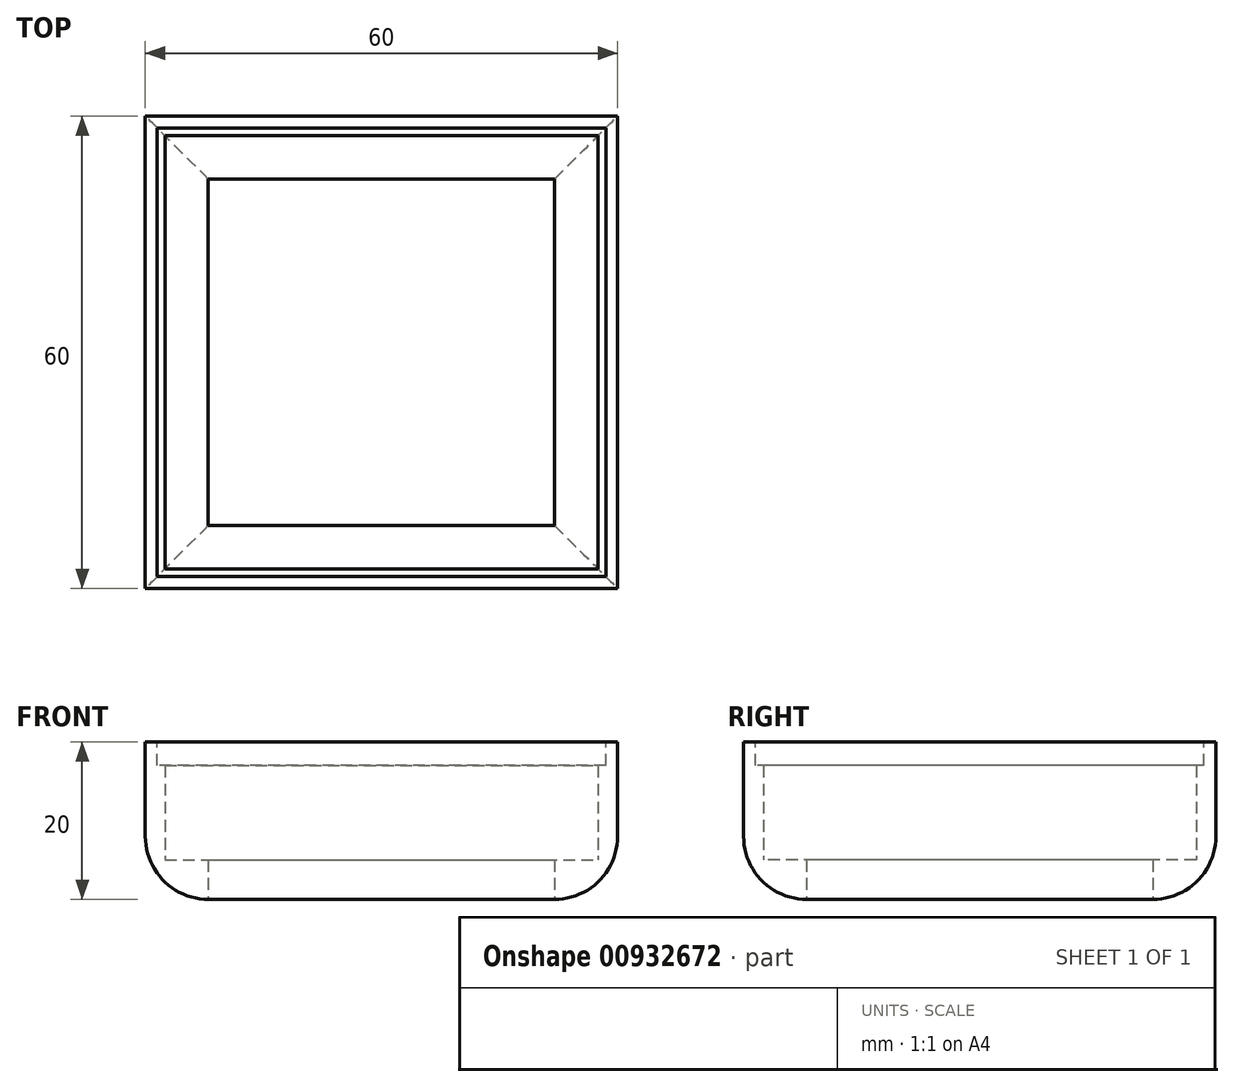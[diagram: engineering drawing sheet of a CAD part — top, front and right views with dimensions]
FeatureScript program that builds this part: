
annotation { "Feature Type Name" : "Feature", "Feature Type Description" : "" }
export const myFeature = defineFeature(function(context is Context, id is Id, definition is map)
    precondition{}
    {
        {
            var Q0;
            Q0=qCreatedBy(makeId("Top.planeOp"),FACE);
            var sketch = newSketch(context, id + "F0", { "sketchPlane" : qUnion([Q0])});
            skLineSegment(sketch, "E0.bottom", {"start": v(-30, 30) * mm, "end": v(30, 30) * mm});
            skLineSegment(sketch, "E0.top", {"start": v(-30, -30) * mm, "end": v(30, -30) * mm});
            skLineSegment(sketch, "E0.left", {"start": v(-30, 30) * mm, "end": v(-30, -30) * mm});
            skLineSegment(sketch, "E0.right", {"start": v(30, 30) * mm, "end": v(30, -30) * mm});
            skPoint(sketch, "E0.middle", {"position": v(0, 0) * mm});
            skLineSegment(sketch, "E1.bottom", {"start": v(-27.5, 27.5) * mm, "end": v(27.5, 27.5) * mm});
            skLineSegment(sketch, "E1.top", {"start": v(-27.5, -27.5) * mm, "end": v(27.5, -27.5) * mm});
            skLineSegment(sketch, "E1.left", {"start": v(-27.5, 27.5) * mm, "end": v(-27.5, -27.5) * mm});
            skLineSegment(sketch, "E1.right", {"start": v(27.5, 27.5) * mm, "end": v(27.5, -27.5) * mm});
            skSolve(sketch);
        }
        {
            var Q0;
            Q0=makeQuery(id+"F0.imprint","IMPRINT",FACE,{"disambiguationData":[TD([[makeQuery(id+"F0.imprint","IMPRINT",EDGE,{"derivedFrom":sQuery(id+"F0.wireOp",EDGE,"E0.bottom")}),-1.0]])]});
            extrude(context, id + "F1", {"entities" : qUnion([Q0]), "depth" : 15 * mm, "offsetDistance" : 25 * mm});
        }
        {
            var Q0;
            Q0=makeQuery(id+"F1.opExtrude","CAP_FACE",FACE,{"disambiguationData":[OSD([sQuery(id+"F0.wireOp",EDGE,"E0.bottom"),sQuery(id+"F0.wireOp",EDGE,"E0.top"),sQuery(id+"F0.wireOp",EDGE,"E0.left"),sQuery(id+"F0.wireOp",EDGE,"E0.right"),sQuery(id+"F0.wireOp",EDGE,"E1.bottom"),sQuery(id+"F0.wireOp",EDGE,"E1.top"),sQuery(id+"F0.wireOp",EDGE,"E1.left"),sQuery(id+"F0.wireOp",EDGE,"E1.right")])],"isStart":true});
            var sketch = newSketch(context, id + "F2", { "sketchPlane" : qUnion([Q0])});
            skLineSegment(sketch, "E2.bottom", {"start": v(30, -30) * mm, "end": v(-30, -30) * mm});
            skLineSegment(sketch, "E2.top", {"start": v(30, 30) * mm, "end": v(-30, 30) * mm});
            skLineSegment(sketch, "E2.left", {"start": v(30, -30) * mm, "end": v(30, 30) * mm});
            skLineSegment(sketch, "E2.right", {"start": v(-30, -30) * mm, "end": v(-30, 30) * mm});
            skSolve(sketch);
        }
        {
            var Q0;
            Q0=makeQuery(id+"F2.imprint","IMPRINT",FACE,{"disambiguationData":[TD([[makeQuery(id+"F2.imprint","IMPRINT",EDGE,{"derivedFrom":sQuery(id+"F2.wireOp",EDGE,"E2.bottom")}),1.0]])]});
            var Q1;
            Q1=makeQuery(id+"F2.imprint","IMPRINT",FACE,{"disambiguationData":[TD([[makeQuery(id+"F2.imprint","IMPRINT",EDGE,{"derivedFrom":makeQuery(id+"F1.opExtrude","CAP_EDGE",EDGE,{"disambiguationData":[OSD([sQuery(id+"F0.wireOp",EDGE,"E1.bottom")])],"isStart":true})}),1.0]])]});
            extrude(context, id + "F3", {"entities" : qUnion([Q0, Q1]), "operationType" : NewBodyOperationType.ADD, "depth" : 5 * mm, "offsetDistance" : 25 * mm});
        }
        {
            var Q0;
            Q0=makeQuery(id+"F1.opExtrude","CAP_FACE",FACE,{"disambiguationData":[OSD([sQuery(id+"F0.wireOp",EDGE,"E0.bottom"),sQuery(id+"F0.wireOp",EDGE,"E0.top"),sQuery(id+"F0.wireOp",EDGE,"E0.left"),sQuery(id+"F0.wireOp",EDGE,"E0.right"),sQuery(id+"F0.wireOp",EDGE,"E1.bottom"),sQuery(id+"F0.wireOp",EDGE,"E1.top"),sQuery(id+"F0.wireOp",EDGE,"E1.left"),sQuery(id+"F0.wireOp",EDGE,"E1.right")])],"isStart":false});
            var sketch = newSketch(context, id + "F4", { "sketchPlane" : qUnion([Q0])});
            skLineSegment(sketch, "E3.bottom", {"start": v(28.5, 28.5) * mm, "end": v(-28.5, 28.5) * mm});
            skLineSegment(sketch, "E3.top", {"start": v(28.5, -28.5) * mm, "end": v(-28.5, -28.5) * mm});
            skLineSegment(sketch, "E3.left", {"start": v(28.5, 28.5) * mm, "end": v(28.5, -28.5) * mm});
            skLineSegment(sketch, "E3.right", {"start": v(-28.5, 28.5) * mm, "end": v(-28.5, -28.5) * mm});
            skPoint(sketch, "E3.middle", {"position": v(0, 0) * mm});
            skSolve(sketch);
        }
        {
            var Q0;
            Q0=makeQuery(id+"F4.imprint","IMPRINT",FACE,{"disambiguationData":[TD([[makeQuery(id+"F4.imprint","IMPRINT",EDGE,{"derivedFrom":sQuery(id+"F4.wireOp",EDGE,"E3.bottom")}),1.0]])]});
            extrude(context, id + "F5", {"entities" : qUnion([Q0]), "operationType" : NewBodyOperationType.REMOVE, "oppositeDirection" : true, "depth" : 3 * mm, "offsetDistance" : 25 * mm});
        }
        {
            var Q0;
            Q0=makeQuery(id+"F3.opExtrude","CAP_EDGE",EDGE,{"disambiguationData":[OSD([sQuery(id+"F2.wireOp",EDGE,"E2.right")])],"isStart":false});
            var Q1;
            Q1=makeQuery(id+"F3.opExtrude","CAP_EDGE",EDGE,{"disambiguationData":[OSD([sQuery(id+"F2.wireOp",EDGE,"E2.left")])],"isStart":false});
            var Q2;
            Q2=makeQuery(id+"F3.opExtrude","CAP_EDGE",EDGE,{"disambiguationData":[OSD([sQuery(id+"F2.wireOp",EDGE,"E2.bottom")])],"isStart":false});
            var Q3;
            Q3=makeQuery(id+"F3.opExtrude","CAP_EDGE",EDGE,{"disambiguationData":[OSD([sQuery(id+"F2.wireOp",EDGE,"E2.top")])],"isStart":false});
            fillet(context, id + "F6", {"entities" : qUnion([Q0, Q1, Q2, Q3]), "tangentPropagation" : true, "radius" : 8 * mm, "defaultsChanged" : false, "vertexSettings" : [], "allowEdgeOverflow" : false});
        }
        {
            var Q0;
            Q0=makeQuery(id+"F3.opExtrude","CAP_FACE",FACE,{"disambiguationData":[OSD([sQuery(id+"F2.wireOp",EDGE,"E2.bottom"),sQuery(id+"F2.wireOp",EDGE,"E2.top"),sQuery(id+"F2.wireOp",EDGE,"E2.left"),sQuery(id+"F2.wireOp",EDGE,"E2.right")])],"isStart":false});
            var sketch = newSketch(context, id + "F7", { "sketchPlane" : qUnion([Q0])});
            skLineSegment(sketch, "E4.bottom", {"start": v(22, -22) * mm, "end": v(-22, -22) * mm});
            skLineSegment(sketch, "E4.top", {"start": v(22, 22) * mm, "end": v(-22, 22) * mm});
            skLineSegment(sketch, "E4.left", {"start": v(22, -22) * mm, "end": v(22, 22) * mm});
            skLineSegment(sketch, "E4.right", {"start": v(-22, -22) * mm, "end": v(-22, 22) * mm});
            skPoint(sketch, "E4.middle", {"position": v(0, 0) * mm});
            skSolve(sketch);
        }
        {
            var Q0;
            Q0=makeQuery(id+"F7.imprint","IMPRINT",FACE,{"disambiguationData":[TD([[makeQuery(id+"F7.imprint","IMPRINT",EDGE,{"derivedFrom":sQuery(id+"F7.wireOp",EDGE,"E4.bottom")}),1.0]])]});
            extrude(context, id + "F8", {"entities" : qUnion([Q0]), "operationType" : NewBodyOperationType.REMOVE, "oppositeDirection" : true, "depth" : 5 * mm, "offsetDistance" : 25 * mm});
        }
    });
